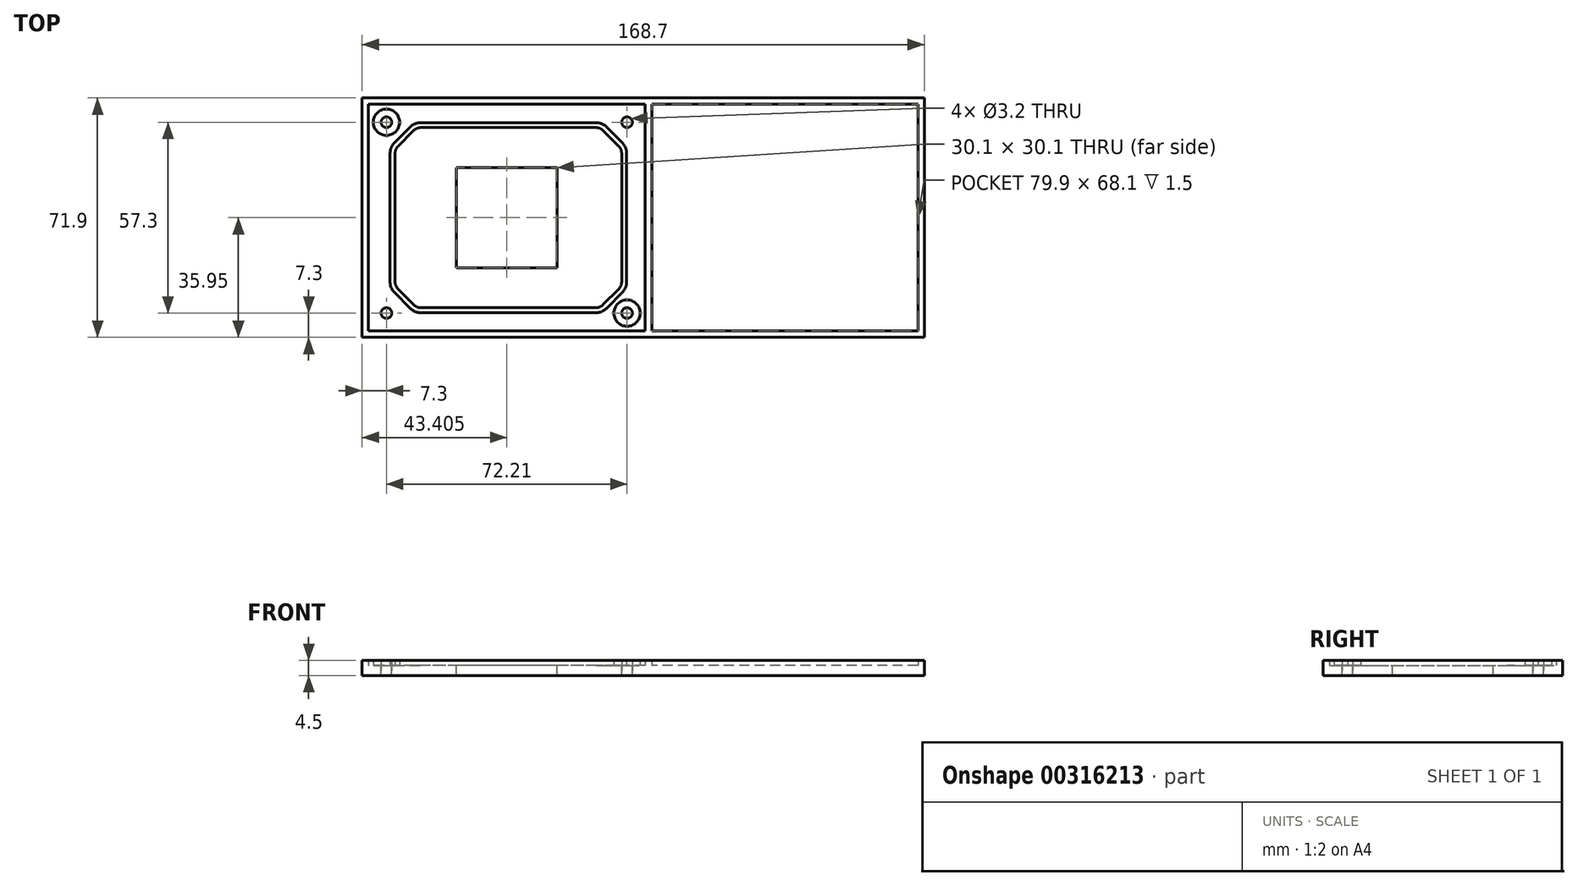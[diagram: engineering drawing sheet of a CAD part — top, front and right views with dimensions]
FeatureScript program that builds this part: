
annotation { "Feature Type Name" : "Feature", "Feature Type Description" : "" }
export const myFeature = defineFeature(function(context is Context, id is Id, definition is map)
    precondition{}
    {
        {
            var Q0;
            Q0=qCreatedBy(makeId("Top.planeOp"),FACE);
            var sketch = newSketch(context, id + "F0", { "sketchPlane" : qUnion([Q0])});
            skLineSegment(sketch, "E0.bottom", {"start": v(84.35, -35.95) * mm, "end": v(-84.35, -35.95) * mm});
            skLineSegment(sketch, "E0.top", {"start": v(84.35, 35.95) * mm, "end": v(-84.35, 35.95) * mm});
            skLineSegment(sketch, "E0.left", {"start": v(84.35, -35.95) * mm, "end": v(84.35, 35.95) * mm});
            skLineSegment(sketch, "E0.right", {"start": v(-84.35, -35.95) * mm, "end": v(-84.35, 35.95) * mm});
            skPoint(sketch, "E0.middle", {"position": v(0, 0) * mm});
            skLineSegment(sketch, "E1.0", {"start": v(82.45, 34.05) * mm, "end": v(2.55, 34.05) * mm});
            skLineSegment(sketch, "E1.1", {"start": v(82.45, -34.05) * mm, "end": v(82.45, 34.05) * mm});
            skLineSegment(sketch, "E1.2", {"start": v(82.45, -34.05) * mm, "end": v(2.55, -34.05) * mm});
            skLineSegment(sketch, "E1.3", {"start": v(-82.45, -34.05) * mm, "end": v(-82.45, 34.05) * mm});
            skLineSegment(sketch, "E2.0", {"start": v(2.55, -34.05) * mm, "end": v(2.55, 34.05) * mm});
            skLineSegment(sketch, "E3.0", {"start": v(0.56, -34.05) * mm, "end": v(0.56, 34.05) * mm});
            skLineSegment(sketch, "E4.trimOffspring", {"start": v(0.56, 34.05) * mm, "end": v(-82.45, 34.05) * mm});
            skLineSegment(sketch, "E5.trimOffspring", {"start": v(0.56, -34.05) * mm, "end": v(-82.45, -34.05) * mm});
            skCircle(sketch, "E6", {"center": v(-77.05, 28.65) * mm, "radius": 3.95 * mm});
            skCircle(sketch, "E7", {"center": v(-77.05, 28.65) * mm, "radius": 1.6 * mm});
            skLineSegment(sketch, "E8", {"start": v(-84.35, 0) * mm, "end": v(84.35, 0) * mm});
            skLineSegment(sketch, "E9", {"start": v(0, 35.95) * mm, "end": v(0, -35.95) * mm, "construction": true});
            skLineSegment(sketch, "E10.0", {"start": v(-40.94, -34.05) * mm, "end": v(-40.95, 34.05) * mm, "construction": true});
            skCircle(sketch, "E11.MirrorC", {"center": v(-77.05, -28.65) * mm, "radius": 1.6 * mm});
            skCircle(sketch, "E12.MirrorC", {"center": v(-77.05, -28.65) * mm, "radius": 3.95 * mm});
            skCircle(sketch, "E13.MirrorC", {"center": v(-4.84, 28.65) * mm, "radius": 1.6 * mm});
            skCircle(sketch, "E14.MirrorC", {"center": v(-4.84, 28.65) * mm, "radius": 3.95 * mm});
            skCircle(sketch, "E15.MirrorC", {"center": v(-4.84, -28.65) * mm, "radius": 3.95 * mm});
            skCircle(sketch, "E16.MirrorC", {"center": v(-4.84, -28.65) * mm, "radius": 1.6 * mm});
            skPoint(sketch, "E17.middle", {"position": v(-40.94, 0) * mm});
            skLineSegment(sketch, "E18.bottom", {"start": v(-25.9, -15.05) * mm, "end": v(-56, -15.05) * mm});
            skLineSegment(sketch, "E18.top", {"start": v(-25.9, 15.05) * mm, "end": v(-56, 15.05) * mm});
            skLineSegment(sketch, "E18.left", {"start": v(-25.9, -15.05) * mm, "end": v(-25.9, 15.05) * mm});
            skLineSegment(sketch, "E18.right", {"start": v(-56, -15.05) * mm, "end": v(-56, 15.05) * mm});
            skLineSegment(sketch, "E19.0", {"start": v(-24, -15.05) * mm, "end": v(-24, 15.05) * mm});
            skLineSegment(sketch, "E20.0", {"start": v(-61, -15.05) * mm, "end": v(-61, 15.05) * mm});
            skLineSegment(sketch, "E21", {"start": v(-6.45, 19.3) * mm, "end": v(-6.45, -19.3) * mm});
            skLineSegment(sketch, "E22", {"start": v(-74.45, 19.3) * mm, "end": v(-74.45, -19.3) * mm});
            skLineSegment(sketch, "E23", {"start": v(-66.7, 27.05) * mm, "end": v(-14.2, 27.05) * mm});
            skLineSegment(sketch, "E24", {"start": v(-66.7, -27.05) * mm, "end": v(-14.2, -27.05) * mm});
            skLineSegment(sketch, "E25", {"start": v(-68.83, 26.17) * mm, "end": v(-73.57, 21.43) * mm});
            skLineSegment(sketch, "E26", {"start": v(-12.07, 26.17) * mm, "end": v(-7.33, 21.43) * mm});
            skLineSegment(sketch, "E27", {"start": v(-7.33, -21.43) * mm, "end": v(-12.07, -26.17) * mm});
            skLineSegment(sketch, "E28", {"start": v(-73.57, -21.43) * mm, "end": v(-68.83, -26.17) * mm});
            skPoint(sketch, "E29.orphan", {"position": v(-74.45, 27.05) * mm});
            skPoint(sketch, "E30.orphan", {"position": v(-6.45, 27.05) * mm});
            skPoint(sketch, "E31.orphan", {"position": v(-6.45, -27.05) * mm});
            skPoint(sketch, "E32.orphan", {"position": v(-74.45, -27.05) * mm});
            skPoint(sketch, "E33.visualSharp", {"position": v(-67.95, 27.05) * mm});
            skArc(sketch, "E33.filletArc", {"start": v(-66.7, 27.05) * mm, "mid": v(-67.86, 26.82) * mm, "end": v(-68.83, 26.17) * mm});
            skPoint(sketch, "E34.visualSharp", {"position": v(-74.45, 20.55) * mm});
            skArc(sketch, "E34.filletArc", {"start": v(-73.57, 21.43) * mm, "mid": v(-74.22, 20.46) * mm, "end": v(-74.45, 19.3) * mm});
            skPoint(sketch, "E35.visualSharp", {"position": v(-12.95, 27.05) * mm});
            skArc(sketch, "E35.filletArc", {"start": v(-12.07, 26.17) * mm, "mid": v(-13.04, 26.82) * mm, "end": v(-14.2, 27.05) * mm});
            skPoint(sketch, "E36.visualSharp", {"position": v(-6.45, 20.55) * mm});
            skArc(sketch, "E36.filletArc", {"start": v(-6.45, 19.3) * mm, "mid": v(-6.68, 20.46) * mm, "end": v(-7.33, 21.43) * mm});
            skPoint(sketch, "E37.visualSharp", {"position": v(-6.45, -20.55) * mm});
            skArc(sketch, "E37.filletArc", {"start": v(-7.33, -21.43) * mm, "mid": v(-6.68, -20.46) * mm, "end": v(-6.45, -19.3) * mm});
            skPoint(sketch, "E38.visualSharp", {"position": v(-12.95, -27.05) * mm});
            skArc(sketch, "E38.filletArc", {"start": v(-14.2, -27.05) * mm, "mid": v(-13.04, -26.82) * mm, "end": v(-12.07, -26.17) * mm});
            skPoint(sketch, "E39.visualSharp", {"position": v(-67.95, -27.05) * mm});
            skArc(sketch, "E39.filletArc", {"start": v(-68.83, -26.17) * mm, "mid": v(-67.86, -26.82) * mm, "end": v(-66.7, -27.05) * mm});
            skPoint(sketch, "E40.visualSharp", {"position": v(-74.45, -20.55) * mm});
            skArc(sketch, "E40.filletArc", {"start": v(-74.45, -19.3) * mm, "mid": v(-74.22, -20.46) * mm, "end": v(-73.57, -21.43) * mm});
            skLineSegment(sketch, "E41.0", {"start": v(-75.95, 19.3) * mm, "end": v(-75.95, -19.3) * mm});
            skArc(sketch, "E41.1", {"start": v(-74.63, 22.49) * mm, "mid": v(-75.6, 21.03) * mm, "end": v(-75.95, 19.3) * mm});
            skLineSegment(sketch, "E41.2", {"start": v(-69.89, 27.23) * mm, "end": v(-74.63, 22.49) * mm});
            skArc(sketch, "E41.3", {"start": v(-66.7, 28.55) * mm, "mid": v(-68.43, 28.2) * mm, "end": v(-69.89, 27.23) * mm});
            skLineSegment(sketch, "E41.4", {"start": v(-66.7, 28.55) * mm, "end": v(-14.2, 28.55) * mm});
            skArc(sketch, "E41.5", {"start": v(-14.2, -28.55) * mm, "mid": v(-12.47, -28.2) * mm, "end": v(-11.01, -27.23) * mm});
            skLineSegment(sketch, "E41.6", {"start": v(-66.7, -28.55) * mm, "end": v(-14.2, -28.55) * mm});
            skArc(sketch, "E41.7", {"start": v(-69.89, -27.23) * mm, "mid": v(-68.43, -28.2) * mm, "end": v(-66.7, -28.55) * mm});
            skLineSegment(sketch, "E41.8", {"start": v(-74.63, -22.49) * mm, "end": v(-69.89, -27.23) * mm});
            skLineSegment(sketch, "E41.9", {"start": v(-6.27, -22.49) * mm, "end": v(-11.01, -27.23) * mm});
            skArc(sketch, "E41.10", {"start": v(-6.27, -22.49) * mm, "mid": v(-5.3, -21.03) * mm, "end": v(-4.95, -19.3) * mm});
            skLineSegment(sketch, "E41.11", {"start": v(-4.95, 19.3) * mm, "end": v(-4.95, -19.3) * mm});
            skArc(sketch, "E41.12", {"start": v(-4.95, 19.3) * mm, "mid": v(-5.3, 21.03) * mm, "end": v(-6.27, 22.49) * mm});
            skLineSegment(sketch, "E41.13", {"start": v(-11.01, 27.23) * mm, "end": v(-6.27, 22.49) * mm});
            skArc(sketch, "E41.14", {"start": v(-75.95, -19.3) * mm, "mid": v(-75.6, -21.03) * mm, "end": v(-74.63, -22.49) * mm});
            skArc(sketch, "E41.15", {"start": v(-11.01, 27.23) * mm, "mid": v(-12.47, 28.2) * mm, "end": v(-14.2, 28.55) * mm});
            skSolve(sketch);
        }
        {
            var Q0;
            Q0=makeQuery(id+"F0.imprint","IMPRINT",FACE,{"disambiguationData":[TD([[makeQuery(id+"F0.imprint","IMPRINT",EDGE,{"derivedFrom":sQuery(id+"F0.wireOp",EDGE,"E0.bottom")}),-1.0]])]});
            var Q1;
            {var subQ13=sQuery(id+"F0.wireOp",EDGE,"E0.top");Q1=makeQuery(id+"F0.imprint","IMPRINT",FACE,{"disambiguationData":[TD([[makeQuery(id+"F0.imprint","IMPRINT",EDGE,{"derivedFrom":subQ13}),1.0]])]});}
            var Q2;
            Q2=makeQuery(id+"F0.imprint","IMPRINT",FACE,{"disambiguationData":[TD([[makeQuery(id+"F0.imprint","IMPRINT",EDGE,{"derivedFrom":sQuery(id+"F0.wireOp",EDGE,"E6")}),1.0]])]});
            var Q3;
            Q3=makeQuery(id+"F0.imprint","IMPRINT",FACE,{"disambiguationData":[TD([[makeQuery(id+"F0.imprint","IMPRINT",EDGE,{"derivedFrom":sQuery(id+"F0.wireOp",EDGE,"E11.MirrorC")}),1.0]])]});
            var Q4;
            Q4=makeQuery(id+"F0.imprint","IMPRINT",FACE,{"disambiguationData":[TD([[makeQuery(id+"F0.imprint","IMPRINT",EDGE,{"derivedFrom":sQuery(id+"F0.wireOp",EDGE,"E13.MirrorC")}),1.0]])]});
            var Q5;
            Q5=makeQuery(id+"F0.imprint","IMPRINT",FACE,{"disambiguationData":[TD([[makeQuery(id+"F0.imprint","IMPRINT",EDGE,{"derivedFrom":sQuery(id+"F0.wireOp",EDGE,"E15.MirrorC")}),1.0]])]});
            var Q6;
            Q6=makeQuery(id+"F0.imprint","IMPRINT",FACE,{"disambiguationData":[TD([[makeQuery(id+"F0.imprint","IMPRINT",EDGE,{"derivedFrom":sQuery(id+"F0.wireOp",EDGE,"E23")}),1.0]])]});
            var Q7;
            Q7=makeQuery(id+"F0.imprint","IMPRINT",FACE,{"disambiguationData":[TD([[makeQuery(id+"F0.imprint","IMPRINT",EDGE,{"derivedFrom":sQuery(id+"F0.wireOp",EDGE,"E24")}),-1.0]])]});
            extrude(context, id + "F1", {"entities" : qUnion([Q0, Q1, Q2, Q3, Q4, Q5, Q6, Q7]), "endBound" : BoundingType.SYMMETRIC, "depth" : 4.5 * mm});
        }
        {
            var Q0;
            Q0=makeQuery(id+"F1.opExtrude","CAP_FACE",FACE,{"disambiguationData":[OSD([sQuery(id+"F0.wireOp",EDGE,"E0.bottom"),sQuery(id+"F0.wireOp",EDGE,"E0.top"),sQuery(id+"F0.wireOp",EDGE,"E0.left"),sQuery(id+"F0.wireOp",EDGE,"E0.right"),sQuery(id+"F0.wireOp",EDGE,"E1.0"),sQuery(id+"F0.wireOp",EDGE,"E1.1"),sQuery(id+"F0.wireOp",EDGE,"E1.2"),sQuery(id+"F0.wireOp",EDGE,"E1.3"),sQuery(id+"F0.wireOp",EDGE,"E2.0"),sQuery(id+"F0.wireOp",EDGE,"E3.0"),sQuery(id+"F0.wireOp",EDGE,"E4.trimOffspring"),sQuery(id+"F0.wireOp",EDGE,"E5.trimOffspring")])],"isStart":true});
            var sketch = newSketch(context, id + "F2", { "sketchPlane" : qUnion([Q0])});
            skLineSegment(sketch, "E42.0", {"start": v(-82.45, 34.05) * mm, "end": v(-82.45, -34.05) * mm});
            skLineSegment(sketch, "E43.0", {"start": v(0.56, -34.05) * mm, "end": v(-82.45, -34.05) * mm});
            skLineSegment(sketch, "E44.0", {"start": v(0.56, 34.05) * mm, "end": v(0.56, -34.05) * mm});
            skLineSegment(sketch, "E45.0", {"start": v(0.56, 34.05) * mm, "end": v(-82.45, 34.05) * mm});
            skLineSegment(sketch, "E46.0", {"start": v(82.45, 34.05) * mm, "end": v(2.55, 34.05) * mm});
            skLineSegment(sketch, "E47.0", {"start": v(2.55, 34.05) * mm, "end": v(2.55, -34.05) * mm});
            skLineSegment(sketch, "E48.0", {"start": v(82.45, -34.05) * mm, "end": v(2.55, -34.05) * mm});
            skLineSegment(sketch, "E49.0", {"start": v(82.45, 34.05) * mm, "end": v(82.45, -34.05) * mm});
            skSolve(sketch);
        }
        {
            var Q0;
            Q0 = qSketchRegion(id + "F2", true);
            extrude(context, id + "F3", {"entities" : qUnion([Q0]), "operationType" : NewBodyOperationType.ADD, "oppositeDirection" : true, "depth" : 3 * mm});
        }
        {
            var Q0;
            Q0=makeQuery(id+"F3.opExtrude","CAP_FACE",FACE,{"disambiguationData":[OSD([sQuery(id+"F2.wireOp",EDGE,"E42.0"),sQuery(id+"F2.wireOp",EDGE,"E43.0"),sQuery(id+"F2.wireOp",EDGE,"E44.0"),sQuery(id+"F2.wireOp",EDGE,"E45.0")])],"isStart":false});
            var sketch = newSketch(context, id + "F4", { "sketchPlane" : qUnion([Q0])});
            skCircle(sketch, "E50.0", {"center": v(-77.05, 28.65) * mm, "radius": 1.6 * mm});
            skCircle(sketch, "E51.0", {"center": v(-4.84, 28.65) * mm, "radius": 1.6 * mm});
            skCircle(sketch, "E52.0", {"center": v(-4.84, -28.65) * mm, "radius": 1.6 * mm});
            skCircle(sketch, "E53.0", {"center": v(-77.05, -28.65) * mm, "radius": 1.6 * mm});
            skLineSegment(sketch, "E54.0", {"start": v(-56, -15.05) * mm, "end": v(-56, 15.05) * mm});
            skLineSegment(sketch, "E55.0", {"start": v(-25.9, 15.05) * mm, "end": v(-56, 15.05) * mm});
            skLineSegment(sketch, "E56.0", {"start": v(-25.9, -15.05) * mm, "end": v(-25.9, 15.05) * mm});
            skLineSegment(sketch, "E57.0", {"start": v(-25.9, -15.05) * mm, "end": v(-56, -15.05) * mm});
            skSolve(sketch);
        }
        {
            var Q0;
            Q0 = qSketchRegion(id + "F4", true);
            extrude(context, id + "F5", {"entities" : qUnion([Q0]), "operationType" : NewBodyOperationType.REMOVE, "oppositeDirection" : true, "depth" : 25 * mm});
        }
    });
